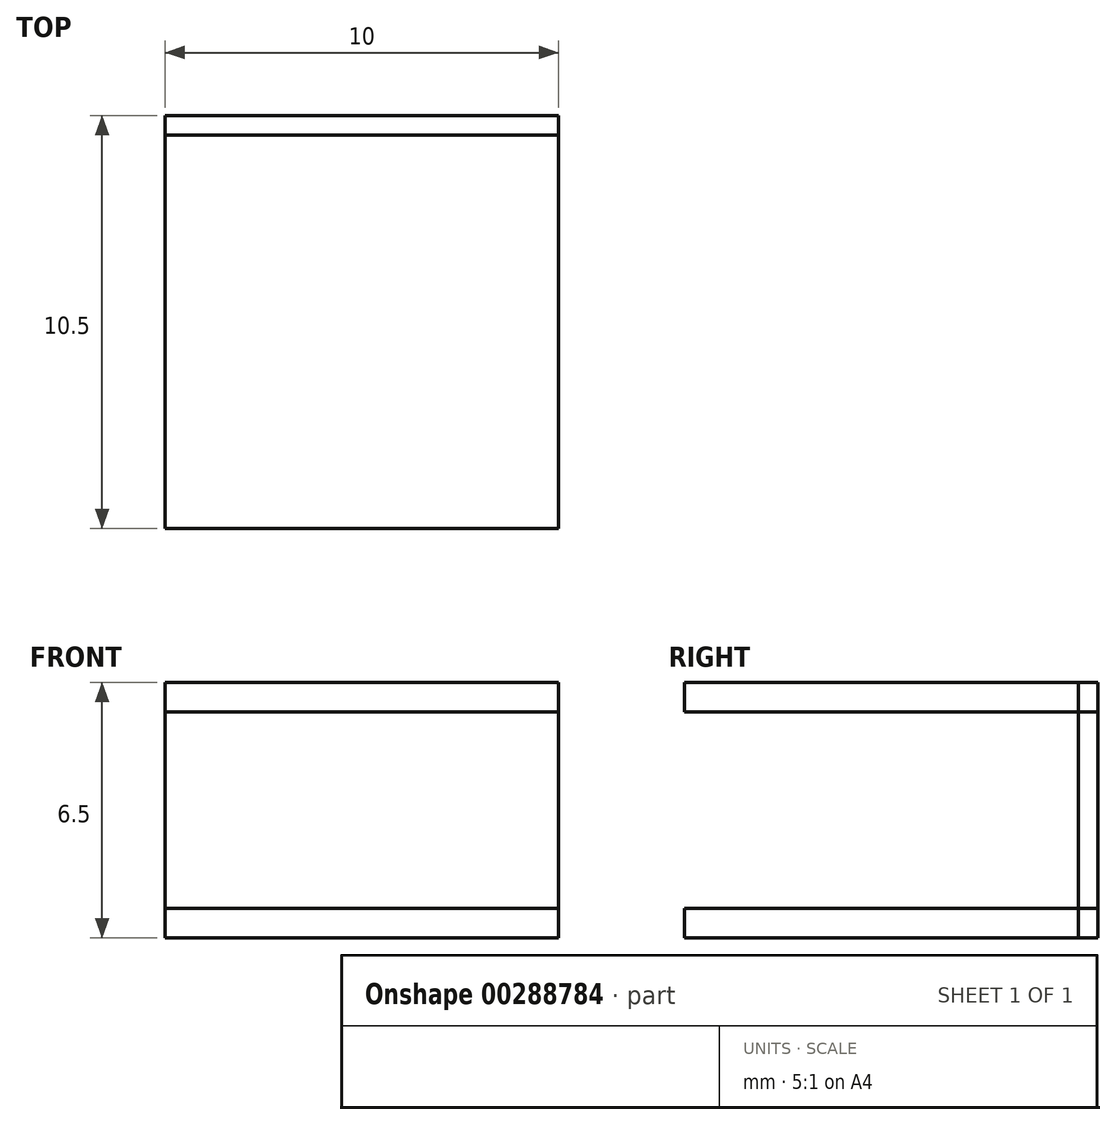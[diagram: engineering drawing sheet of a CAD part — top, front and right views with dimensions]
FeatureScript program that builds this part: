
annotation { "Feature Type Name" : "Feature", "Feature Type Description" : "" }
export const myFeature = defineFeature(function(context is Context, id is Id, definition is map)
    precondition{}
    {
        {
            var Q0;
            Q0=qCreatedBy(makeId("Front.planeOp"),FACE);
            var sketch = newSketch(context, id + "F0", { "sketchPlane" : qUnion([Q0])});
            skLineSegment(sketch, "E0.bottom", {"start": v(0, 0) * mm, "end": v(10, 0) * mm});
            skLineSegment(sketch, "E0.top", {"start": v(0, 5) * mm, "end": v(10, 5) * mm});
            skLineSegment(sketch, "E0.left", {"start": v(0, 0) * mm, "end": v(0, 5) * mm});
            skLineSegment(sketch, "E0.right", {"start": v(10, 0) * mm, "end": v(10, 5) * mm});
            skLineSegment(sketch, "E1.bottom", {"start": v(10, 5.88) * mm, "end": v(0, 5.88) * mm});
            skLineSegment(sketch, "E1.top", {"start": v(10, -1.1) * mm, "end": v(0, -1.1) * mm});
            skLineSegment(sketch, "E1.left", {"start": v(10, 5.88) * mm, "end": v(10, -1.1) * mm});
            skLineSegment(sketch, "E1.right", {"start": v(0, 5.88) * mm, "end": v(0, -1.1) * mm});
            skPoint(sketch, "E1.middle", {"position": v(5, 2.4) * mm});
            skSolve(sketch);
        }
        {
            var Q0;
            {var subQ0=sQuery(id+"F0.wireOp",EDGE,"E1.left");var subQ1=sQuery(id+"F0.wireOp",EDGE,"E0.bottom");var subQ2=makeQuery(id+"F0.imprint","INTERSECT",VERTEX,{"derivedFrom":[subQ1,subQ0]});Q0=makeQuery(id+"F0.imprint","IMPRINT",FACE,{"disambiguationData":[TD([[makeQuery(id+"F0.imprint","IMPRINT",EDGE,{"disambiguationData":[TD([[subQ2,1.0]])],"derivedFrom":subQ1}),1.0]])]});}
            extrude(context, id + "F1", {"entities" : qUnion([Q0]), "depth" : 0.5 * mm});
        }
        {
            var Q0;
            Q0=makeQuery(id+"F1.opExtrude","CAP_FACE",FACE,{"disambiguationData":[OSD([sQuery(id+"F0.wireOp",EDGE,"E0.bottom"),sQuery(id+"F0.wireOp",EDGE,"E0.top"),sQuery(id+"F0.wireOp",EDGE,"E1.left"),sQuery(id+"F0.wireOp",EDGE,"E1.right")])],"isStart":false});
            var sketch = newSketch(context, id + "F2", { "sketchPlane" : qUnion([Q0])});
            skLineSegment(sketch, "E2.bottom", {"start": v(0, 5) * mm, "end": v(10, 5) * mm});
            skLineSegment(sketch, "E2.top", {"start": v(0, 5.75) * mm, "end": v(10, 5.75) * mm});
            skLineSegment(sketch, "E2.left", {"start": v(0, 5) * mm, "end": v(0, 5.75) * mm});
            skLineSegment(sketch, "E2.right", {"start": v(10, 5) * mm, "end": v(10, 5.75) * mm});
            skSolve(sketch);
        }
        {
            var Q0;
            Q0=makeQuery(id+"F2.imprint","IMPRINT",FACE,{"disambiguationData":[TD([[makeQuery(id+"F2.imprint","IMPRINT",EDGE,{"derivedFrom":sQuery(id+"F2.wireOp",EDGE,"E2.bottom")}),-1.0]])]});
            var sketch = newSketch(context, id + "F3", { "sketchPlane" : qUnion([Q0])});
            skLineSegment(sketch, "E3.bottom", {"start": v(0, 0) * mm, "end": v(10, 0) * mm});
            skLineSegment(sketch, "E3.top", {"start": v(0, -0.75) * mm, "end": v(10, -0.75) * mm});
            skLineSegment(sketch, "E3.left", {"start": v(0, 0) * mm, "end": v(0, -0.75) * mm});
            skLineSegment(sketch, "E3.right", {"start": v(10, 0) * mm, "end": v(10, -0.75) * mm});
            skSolve(sketch);
        }
        {
            var Q0;
            Q0=makeQuery(id+"F2.imprint","IMPRINT",FACE,{"disambiguationData":[TD([[makeQuery(id+"F2.imprint","IMPRINT",EDGE,{"derivedFrom":sQuery(id+"F2.wireOp",EDGE,"E2.bottom")}),1.0]])]});
            var Q1;
            Q1=makeQuery(id+"F3.imprint","IMPRINT",FACE,{"disambiguationData":[TD([[makeQuery(id+"F3.imprint","IMPRINT",EDGE,{"derivedFrom":sQuery(id+"F3.wireOp",EDGE,"E3.top")}),1.0]])]});
            extrude(context, id + "F4", {"entities" : qUnion([Q0, Q1]), "depth" : 10 * mm});
        }
        {
            var Q0;
            Q0=makeQuery(id+"F4.opExtrude","CAP_FACE",FACE,{"disambiguationData":[OSD([sQuery(id+"F2.wireOp",EDGE,"E2.bottom"),sQuery(id+"F2.wireOp",EDGE,"E2.top"),sQuery(id+"F2.wireOp",EDGE,"E2.left"),sQuery(id+"F2.wireOp",EDGE,"E2.right")])],"isStart":true});
            var Q1;
            Q1=makeQuery(id+"F4.opExtrude","CAP_FACE",FACE,{"disambiguationData":[OSD([sQuery(id+"F3.wireOp",EDGE,"E3.bottom"),sQuery(id+"F3.wireOp",EDGE,"E3.top"),sQuery(id+"F3.wireOp",EDGE,"E3.left"),sQuery(id+"F3.wireOp",EDGE,"E3.right")])],"isStart":true});
            extrude(context, id + "F5", {"entities" : qUnion([Q0, Q1]), "depth" : 0.5 * mm});
        }
    });
